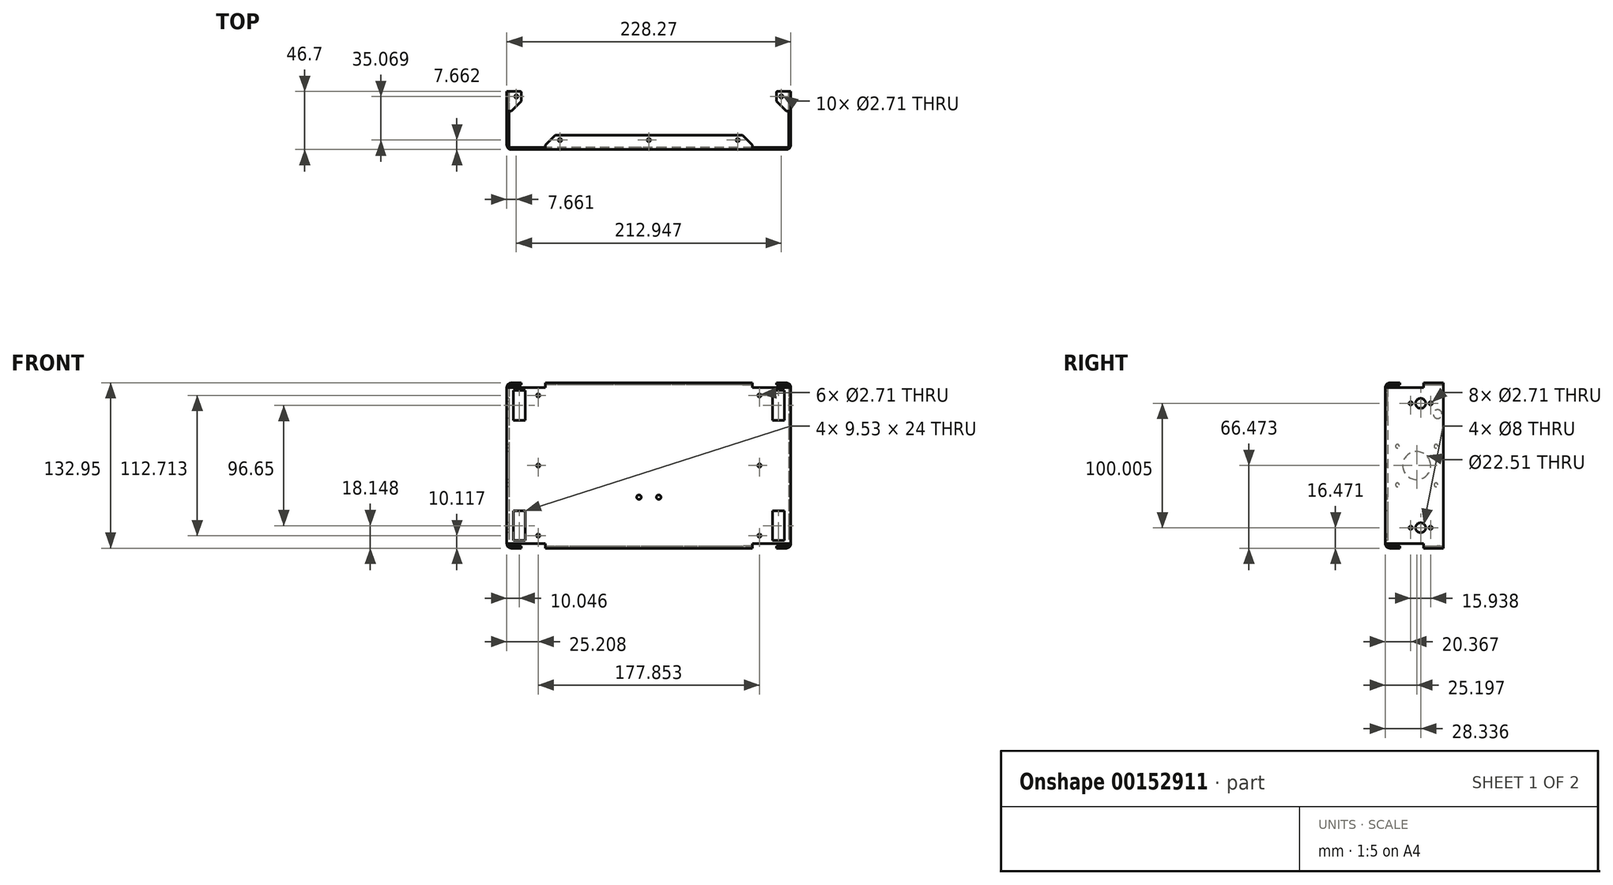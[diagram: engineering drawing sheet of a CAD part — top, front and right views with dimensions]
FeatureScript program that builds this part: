
annotation { "Feature Type Name" : "Feature", "Feature Type Description" : "" }
export const myFeature = defineFeature(function(context is Context, id is Id, definition is map)
    precondition{}
    {
        {
            var Q0;
            Q0=qCreatedBy(makeId("Top.planeOp"),FACE);
            var sketch = newSketch(context, id + "F0", { "sketchPlane" : qUnion([Q0])});
            skLineSegment(sketch, "E0.bottom", {"start": v(0, 0) * mm, "end": v(-224.85, 0) * mm});
            skLineSegment(sketch, "E0.top", {"start": v(1.7, -1.7) * mm, "end": v(-226.56, -1.7) * mm});
            skLineSegment(sketch, "E1.top", {"start": v(-224.85, 44.99) * mm, "end": v(-226.56, 44.99) * mm});
            skLineSegment(sketch, "E1.left", {"start": v(-224.85, 0) * mm, "end": v(-224.85, 44.99) * mm});
            skLineSegment(sketch, "E1.right", {"start": v(-226.56, -1.7) * mm, "end": v(-226.56, 44.99) * mm});
            skLineSegment(sketch, "E2.top", {"start": v(0, 44.99) * mm, "end": v(1.7, 44.99) * mm});
            skLineSegment(sketch, "E2.left", {"start": v(0, 0) * mm, "end": v(0, 44.99) * mm});
            skLineSegment(sketch, "E2.right", {"start": v(1.7, -1.7) * mm, "end": v(1.7, 44.99) * mm});
            skLineSegment(sketch, "E3", {"start": v(-112.43, 0) * mm, "end": v(-112.43, -1.7) * mm, "construction": true});
            skSolve(sketch);
        }
        {
            var Q0;
            Q0 = qSketchRegion(id + "F0", true);
            extrude(context, id + "F1", {"entities" : qUnion([Q0]), "depth" : 125.57 * mm});
        }
        {
            var Q0;
            Q0=makeQuery(id+"F1.opExtrude","CAP_FACE",FACE,{"disambiguationData":[OSD([sQuery(id+"F0.wireOp",EDGE,"E0.bottom"),sQuery(id+"F0.wireOp",EDGE,"E0.top"),sQuery(id+"F0.wireOp",EDGE,"E1.top"),sQuery(id+"F0.wireOp",EDGE,"E1.left"),sQuery(id+"F0.wireOp",EDGE,"E1.right"),sQuery(id+"F0.wireOp",EDGE,"E2.top"),sQuery(id+"F0.wireOp",EDGE,"E2.left"),sQuery(id+"F0.wireOp",EDGE,"E2.right")])],"isStart":true});
            var sketch = newSketch(context, id + "F2", { "sketchPlane" : qUnion([Q0])});
            skLineSegment(sketch, "E4.bottom", {"start": v(1.7, -44.99) * mm, "end": v(0, -44.99) * mm});
            skLineSegment(sketch, "E4.top", {"start": v(1.7, -29.11) * mm, "end": v(0, -29.11) * mm});
            skLineSegment(sketch, "E4.left", {"start": v(1.7, -44.99) * mm, "end": v(1.7, -29.11) * mm});
            skLineSegment(sketch, "E4.right", {"start": v(0, -44.99) * mm, "end": v(0, -29.11) * mm});
            skLineSegment(sketch, "E5.bottom", {"start": v(-29.11, 0) * mm, "end": v(-195.74, 0) * mm});
            skLineSegment(sketch, "E5.top", {"start": v(-29.11, 1.7) * mm, "end": v(-195.74, 1.7) * mm});
            skLineSegment(sketch, "E5.left", {"start": v(-29.11, 0) * mm, "end": v(-29.11, 1.7) * mm});
            skLineSegment(sketch, "E5.right", {"start": v(-195.74, 0) * mm, "end": v(-195.74, 1.7) * mm});
            skLineSegment(sketch, "E6.bottom", {"start": v(-224.85, -44.99) * mm, "end": v(-226.56, -44.99) * mm});
            skLineSegment(sketch, "E6.top", {"start": v(-224.85, -29.11) * mm, "end": v(-226.56, -29.11) * mm});
            skLineSegment(sketch, "E6.left", {"start": v(-224.85, -44.99) * mm, "end": v(-224.85, -29.11) * mm});
            skLineSegment(sketch, "E6.right", {"start": v(-226.56, -44.99) * mm, "end": v(-226.56, -29.11) * mm});
            skPoint(sketch, "E7", {"position": v(-112.43, 0) * mm});
            skLineSegment(sketch, "E8.top", {"start": v(-195.74, -29.11) * mm, "end": v(-224.85, -29.11) * mm, "construction": true});
            skLineSegment(sketch, "E8.left", {"start": v(-195.74, 0) * mm, "end": v(-195.74, -29.11) * mm, "construction": true});
            skSolve(sketch);
        }
        {
            var Q0;
            Q0 = qSketchRegion(id + "F2", true);
            extrude(context, id + "F3", {"entities" : qUnion([Q0]), "operationType" : NewBodyOperationType.ADD, "depth" : 3.7 * mm});
        }
        {
            var Q0;
            Q0=makeQuery(id+"F1.opExtrude","CAP_FACE",FACE,{"disambiguationData":[OSD([sQuery(id+"F0.wireOp",EDGE,"E0.bottom"),sQuery(id+"F0.wireOp",EDGE,"E0.top"),sQuery(id+"F0.wireOp",EDGE,"E1.top"),sQuery(id+"F0.wireOp",EDGE,"E1.left"),sQuery(id+"F0.wireOp",EDGE,"E1.right"),sQuery(id+"F0.wireOp",EDGE,"E2.top"),sQuery(id+"F0.wireOp",EDGE,"E2.left"),sQuery(id+"F0.wireOp",EDGE,"E2.right")])],"isStart":false});
            var sketch = newSketch(context, id + "F4", { "sketchPlane" : qUnion([Q0])});
            skLineSegment(sketch, "E9.bottom", {"start": v(-226.56, 44.99) * mm, "end": v(-224.85, 44.99) * mm});
            skLineSegment(sketch, "E9.top", {"start": v(-226.56, 29.11) * mm, "end": v(-224.85, 29.11) * mm});
            skLineSegment(sketch, "E9.left", {"start": v(-226.56, 44.99) * mm, "end": v(-226.56, 29.11) * mm});
            skLineSegment(sketch, "E9.right", {"start": v(-224.85, 44.99) * mm, "end": v(-224.85, 29.11) * mm});
            skLineSegment(sketch, "E10.bottom", {"start": v(0, 44.99) * mm, "end": v(1.7, 44.99) * mm});
            skLineSegment(sketch, "E10.top", {"start": v(0, 29.11) * mm, "end": v(1.7, 29.11) * mm});
            skLineSegment(sketch, "E10.left", {"start": v(0, 44.99) * mm, "end": v(0, 29.11) * mm});
            skLineSegment(sketch, "E10.right", {"start": v(1.7, 44.99) * mm, "end": v(1.7, 29.11) * mm});
            skLineSegment(sketch, "E11.bottom", {"start": v(-29.11, -1.7) * mm, "end": v(-195.74, -1.7) * mm});
            skLineSegment(sketch, "E11.top", {"start": v(-29.11, 0) * mm, "end": v(-195.74, 0) * mm});
            skLineSegment(sketch, "E11.left", {"start": v(-29.11, -1.7) * mm, "end": v(-29.11, 0) * mm});
            skLineSegment(sketch, "E11.right", {"start": v(-195.74, -1.7) * mm, "end": v(-195.74, 0) * mm});
            skSolve(sketch);
        }
        {
            var Q0;
            Q0 = qSketchRegion(id + "F4", true);
            extrude(context, id + "F5", {"entities" : qUnion([Q0]), "operationType" : NewBodyOperationType.ADD, "depth" : 3.7 * mm});
        }
        {
            var Q0;
            Q0=makeQuery(id+"F5.boolean.opBoolean","MERGE",FACE,{"derivedFrom":[makeQuery(id+"F3.boolean.opBoolean","MERGE",FACE,{"derivedFrom":[makeQuery(id+"F1.opExtrude","SWEPT_FACE",FACE,{"disambiguationData":[OSD([sQuery(id+"F0.wireOp",EDGE,"E0.bottom")])]}),makeQuery(id+"F3.opExtrude","SWEPT_FACE",FACE,{"disambiguationData":[OSD([sQuery(id+"F2.wireOp",EDGE,"E5.bottom")])]})]}),makeQuery(id+"F5.opExtrude","SWEPT_FACE",FACE,{"disambiguationData":[OSD([sQuery(id+"F4.wireOp",EDGE,"E11.top")])]})]});
            var sketch = newSketch(context, id + "F6", { "sketchPlane" : qUnion([Q0])});
            skLineSegment(sketch, "E12.bottom", {"start": v(195.74, -3.7) * mm, "end": v(29.11, -3.7) * mm});
            skLineSegment(sketch, "E12.top", {"start": v(195.74, -1.98) * mm, "end": v(29.11, -1.98) * mm});
            skLineSegment(sketch, "E12.left", {"start": v(195.74, -3.7) * mm, "end": v(195.74, -1.98) * mm});
            skLineSegment(sketch, "E12.right", {"start": v(29.11, -3.7) * mm, "end": v(29.11, -1.98) * mm});
            skLineSegment(sketch, "E13.bottom", {"start": v(29.11, 129.26) * mm, "end": v(195.74, 129.26) * mm});
            skLineSegment(sketch, "E13.top", {"start": v(29.11, 127.55) * mm, "end": v(195.74, 127.55) * mm});
            skLineSegment(sketch, "E13.left", {"start": v(29.11, 129.26) * mm, "end": v(29.11, 127.55) * mm});
            skLineSegment(sketch, "E13.right", {"start": v(195.74, 129.26) * mm, "end": v(195.74, 127.55) * mm});
            skSolve(sketch);
        }
        {
            var Q0;
            Q0 = qSketchRegion(id + "F6", true);
            extrude(context, id + "F7", {"entities" : qUnion([Q0]), "operationType" : NewBodyOperationType.ADD, "depth" : 9.92 * mm});
        }
        {
            var Q0;
            Q0=makeQuery(id+"F5.boolean.opBoolean","MERGE",FACE,{"derivedFrom":[makeQuery(id+"F3.boolean.opBoolean","MERGE",FACE,{"derivedFrom":[makeQuery(id+"F1.opExtrude","SWEPT_FACE",FACE,{"disambiguationData":[OSD([sQuery(id+"F0.wireOp",EDGE,"E1.left")])]}),makeQuery(id+"F3.opExtrude","SWEPT_FACE",FACE,{"disambiguationData":[OSD([sQuery(id+"F2.wireOp",EDGE,"E6.left")])]})]}),makeQuery(id+"F5.opExtrude","SWEPT_FACE",FACE,{"disambiguationData":[OSD([sQuery(id+"F4.wireOp",EDGE,"E9.right")])]})]});
            var sketch = newSketch(context, id + "F8", { "sketchPlane" : qUnion([Q0])});
            skLineSegment(sketch, "E14.bottom", {"start": v(29.11, 129.26) * mm, "end": v(44.99, 129.26) * mm});
            skLineSegment(sketch, "E14.top", {"start": v(29.11, 127.55) * mm, "end": v(44.99, 127.55) * mm});
            skLineSegment(sketch, "E14.left", {"start": v(29.11, 129.26) * mm, "end": v(29.11, 127.55) * mm});
            skLineSegment(sketch, "E14.right", {"start": v(44.99, 129.26) * mm, "end": v(44.99, 127.55) * mm});
            skLineSegment(sketch, "E15.bottom", {"start": v(29.11, -3.7) * mm, "end": v(44.99, -3.7) * mm});
            skLineSegment(sketch, "E15.top", {"start": v(29.11, -1.98) * mm, "end": v(44.99, -1.98) * mm});
            skLineSegment(sketch, "E15.left", {"start": v(29.11, -3.7) * mm, "end": v(29.11, -1.98) * mm});
            skLineSegment(sketch, "E15.right", {"start": v(44.99, -3.7) * mm, "end": v(44.99, -1.98) * mm});
            skSolve(sketch);
        }
        {
            var Q0;
            Q0 = qSketchRegion(id + "F8", true);
            extrude(context, id + "F9", {"entities" : qUnion([Q0]), "operationType" : NewBodyOperationType.ADD, "depth" : 9.92 * mm});
        }
        {
            var Q0;
            Q0=makeQuery(id+"F5.boolean.opBoolean","MERGE",FACE,{"derivedFrom":[makeQuery(id+"F3.boolean.opBoolean","MERGE",FACE,{"derivedFrom":[makeQuery(id+"F1.opExtrude","SWEPT_FACE",FACE,{"disambiguationData":[OSD([sQuery(id+"F0.wireOp",EDGE,"E2.left")])]}),makeQuery(id+"F3.opExtrude","SWEPT_FACE",FACE,{"disambiguationData":[OSD([sQuery(id+"F2.wireOp",EDGE,"E4.right")])]})]}),makeQuery(id+"F5.opExtrude","SWEPT_FACE",FACE,{"disambiguationData":[OSD([sQuery(id+"F4.wireOp",EDGE,"E10.left")])]})]});
            var sketch = newSketch(context, id + "F10", { "sketchPlane" : qUnion([Q0])});
            skLineSegment(sketch, "E16.bottom", {"start": v(-29.11, -3.7) * mm, "end": v(-44.99, -3.7) * mm});
            skLineSegment(sketch, "E16.top", {"start": v(-29.11, -1.98) * mm, "end": v(-44.99, -1.98) * mm});
            skLineSegment(sketch, "E16.left", {"start": v(-29.11, -3.7) * mm, "end": v(-29.11, -1.98) * mm});
            skLineSegment(sketch, "E16.right", {"start": v(-44.99, -3.7) * mm, "end": v(-44.99, -1.98) * mm});
            skLineSegment(sketch, "E17.bottom", {"start": v(-29.11, 129.26) * mm, "end": v(-44.99, 129.26) * mm});
            skLineSegment(sketch, "E17.top", {"start": v(-29.11, 127.55) * mm, "end": v(-44.99, 127.55) * mm});
            skLineSegment(sketch, "E17.left", {"start": v(-29.11, 129.26) * mm, "end": v(-29.11, 127.55) * mm});
            skLineSegment(sketch, "E17.right", {"start": v(-44.99, 129.26) * mm, "end": v(-44.99, 127.55) * mm});
            skSolve(sketch);
        }
        {
            var Q0;
            Q0 = qSketchRegion(id + "F10", true);
            extrude(context, id + "F11", {"entities" : qUnion([Q0]), "operationType" : NewBodyOperationType.ADD, "depth" : 9.92 * mm});
        }
        {
            var Q0;
            Q0=makeQuery(id+"F11.opExtrude","CAP_EDGE",EDGE,{"disambiguationData":[OSD([sQuery(id+"F10.wireOp",EDGE,"E17.top")])],"isStart":true});
            var Q1;
            Q1=makeQuery(id+"F7.opExtrude","CAP_EDGE",EDGE,{"disambiguationData":[OSD([sQuery(id+"F6.wireOp",EDGE,"E13.top")])],"isStart":true});
            var Q2;
            Q2=makeQuery(id+"F9.opExtrude","CAP_EDGE",EDGE,{"disambiguationData":[OSD([sQuery(id+"F8.wireOp",EDGE,"E14.top")])],"isStart":true});
            var Q3;
            Q3=makeQuery(id+"F9.opExtrude","CAP_EDGE",EDGE,{"disambiguationData":[OSD([sQuery(id+"F8.wireOp",EDGE,"E15.top")])],"isStart":true});
            var Q4;
            Q4=makeQuery(id+"F7.opExtrude","CAP_EDGE",EDGE,{"disambiguationData":[OSD([sQuery(id+"F6.wireOp",EDGE,"E12.top")])],"isStart":true});
            var Q5;
            Q5=makeQuery(id+"F11.opExtrude","CAP_EDGE",EDGE,{"disambiguationData":[OSD([sQuery(id+"F10.wireOp",EDGE,"E16.top")])],"isStart":true});
            var Q6;
            Q6=makeQuery(id+"F1.opExtrude","SWEPT_EDGE",EDGE,{"disambiguationData":[OSD([sQuery(id+"F0.wireOp",EDGE,"E0.bottom"),sQuery(id+"F0.wireOp",EDGE,"E2.left")])]});
            var Q7;
            Q7=makeQuery(id+"F1.opExtrude","SWEPT_EDGE",EDGE,{"disambiguationData":[OSD([sQuery(id+"F0.wireOp",EDGE,"E0.bottom"),sQuery(id+"F0.wireOp",EDGE,"E1.left")])]});
            fillet(context, id + "F12", {"entities" : qUnion([Q0, Q1, Q2, Q3, Q4, Q5, Q6, Q7]), "radius" : 1.98 * mm, "tangentPropagation" : true, "allowEdgeOverflow" : false});
        }
        {
            var Q0;
            Q0=makeQuery(id+"F3.opExtrude","CAP_EDGE",EDGE,{"disambiguationData":[OSD([sQuery(id+"F2.wireOp",EDGE,"E6.right")])],"isStart":false});
            var Q1;
            Q1=makeQuery(id+"F3.opExtrude","CAP_EDGE",EDGE,{"disambiguationData":[OSD([sQuery(id+"F2.wireOp",EDGE,"E5.top")])],"isStart":false});
            var Q2;
            Q2=makeQuery(id+"F1.opExtrude","SWEPT_EDGE",EDGE,{"disambiguationData":[OSD([sQuery(id+"F0.wireOp",EDGE,"E0.top"),sQuery(id+"F0.wireOp",EDGE,"E1.right")])]});
            var Q3;
            Q3=makeQuery(id+"F5.opExtrude","CAP_EDGE",EDGE,{"disambiguationData":[OSD([sQuery(id+"F4.wireOp",EDGE,"E11.bottom")])],"isStart":false});
            var Q4;
            Q4=makeQuery(id+"F5.opExtrude","CAP_EDGE",EDGE,{"disambiguationData":[OSD([sQuery(id+"F4.wireOp",EDGE,"E9.left")])],"isStart":false});
            var Q5;
            Q5=makeQuery(id+"F3.opExtrude","CAP_EDGE",EDGE,{"disambiguationData":[OSD([sQuery(id+"F2.wireOp",EDGE,"E4.left")])],"isStart":false});
            var Q6;
            Q6=makeQuery(id+"F1.opExtrude","SWEPT_EDGE",EDGE,{"disambiguationData":[OSD([sQuery(id+"F0.wireOp",EDGE,"E0.top"),sQuery(id+"F0.wireOp",EDGE,"E2.right")])]});
            var Q7;
            Q7=makeQuery(id+"F5.opExtrude","CAP_EDGE",EDGE,{"disambiguationData":[OSD([sQuery(id+"F4.wireOp",EDGE,"E10.right")])],"isStart":false});
            fillet(context, id + "F13", {"entities" : qUnion([Q0, Q1, Q2, Q3, Q4, Q5, Q6, Q7]), "radius" : 3.7 * mm, "tangentPropagation" : true, "allowEdgeOverflow" : false});
        }
        {
            var Q0;
            Q0=makeQuery(id+"F9.opExtrude","CAP_EDGE",EDGE,{"disambiguationData":[OSD([sQuery(id+"F8.wireOp",EDGE,"E14.left")])],"isStart":false});
            var Q1;
            Q1=makeQuery(id+"F7.opExtrude","CAP_EDGE",EDGE,{"disambiguationData":[OSD([sQuery(id+"F6.wireOp",EDGE,"E13.right")])],"isStart":false});
            var Q2;
            Q2=makeQuery(id+"F7.opExtrude","CAP_EDGE",EDGE,{"disambiguationData":[OSD([sQuery(id+"F6.wireOp",EDGE,"E13.left")])],"isStart":false});
            var Q3;
            Q3=makeQuery(id+"F11.opExtrude","CAP_EDGE",EDGE,{"disambiguationData":[OSD([sQuery(id+"F10.wireOp",EDGE,"E17.left")])],"isStart":false});
            var Q4;
            Q4=makeQuery(id+"F7.opExtrude","CAP_EDGE",EDGE,{"disambiguationData":[OSD([sQuery(id+"F6.wireOp",EDGE,"E12.right")])],"isStart":false});
            var Q5;
            Q5=makeQuery(id+"F11.opExtrude","CAP_EDGE",EDGE,{"disambiguationData":[OSD([sQuery(id+"F10.wireOp",EDGE,"E16.left")])],"isStart":false});
            var Q6;
            Q6=makeQuery(id+"F9.opExtrude","CAP_EDGE",EDGE,{"disambiguationData":[OSD([sQuery(id+"F8.wireOp",EDGE,"E15.left")])],"isStart":false});
            var Q7;
            Q7=makeQuery(id+"F7.opExtrude","CAP_EDGE",EDGE,{"disambiguationData":[OSD([sQuery(id+"F6.wireOp",EDGE,"E12.left")])],"isStart":false});
            chamfer(context, id + "F14", {"entities" : qUnion([Q0, Q1, Q2, Q3, Q4, Q5, Q6, Q7]), "width" : 7.94 * mm, "tangentPropagation" : true});
        }
        {
            var Q0;
            Q0=makeQuery(id+"F7.boolean.opBoolean","MERGE",FACE,{"derivedFrom":[makeQuery(id+"F3.opExtrude","CAP_FACE",FACE,{"disambiguationData":[OSD([sQuery(id+"F2.wireOp",EDGE,"E5.bottom"),sQuery(id+"F2.wireOp",EDGE,"E5.top"),sQuery(id+"F2.wireOp",EDGE,"E5.left"),sQuery(id+"F2.wireOp",EDGE,"E5.right")])],"isStart":false}),makeQuery(id+"F7.opExtrude","SWEPT_FACE",FACE,{"disambiguationData":[OSD([sQuery(id+"F6.wireOp",EDGE,"E12.bottom")])]})]});
            var sketch = newSketch(context, id + "F15", { "sketchPlane" : qUnion([Q0])});
            skLineSegment(sketch, "E18", {"start": v(-33.08, -5.95) * mm, "end": v(-41.02, -5.95) * mm, "construction": true});
            skLineSegment(sketch, "E19", {"start": v(-41.02, -5.95) * mm, "end": v(-112.43, -5.95) * mm, "construction": true});
            skLineSegment(sketch, "E20", {"start": v(-112.43, -5.95) * mm, "end": v(-183.83, -5.95) * mm, "construction": true});
            skLineSegment(sketch, "E21", {"start": v(-183.83, -5.95) * mm, "end": v(-191.77, -5.95) * mm, "construction": true});
            skCircle(sketch, "E22", {"center": v(-41.02, -5.95) * mm, "radius": 1.35 * mm});
            skCircle(sketch, "E23", {"center": v(-112.43, -5.95) * mm, "radius": 1.35 * mm});
            skCircle(sketch, "E24", {"center": v(-183.83, -5.95) * mm, "radius": 1.35 * mm});
            skLineSegment(sketch, "E25", {"start": v(-5.95, -33.08) * mm, "end": v(-5.95, -41.02) * mm, "construction": true});
            skLineSegment(sketch, "E26", {"start": v(-218.9, -33.08) * mm, "end": v(-218.9, -41.02) * mm, "construction": true});
            skCircle(sketch, "E27", {"center": v(-218.9, -41.02) * mm, "radius": 1.35 * mm});
            skCircle(sketch, "E28", {"center": v(-5.95, -41.02) * mm, "radius": 1.35 * mm});
            skSolve(sketch);
        }
        {
            var Q0;
            Q0 = qSketchRegion(id + "F15", true);
            var Q1;
            Q1=makeQuery(id+"F7.boolean.opBoolean","MERGE",FACE,{"derivedFrom":[makeQuery(id+"F5.opExtrude","CAP_FACE",FACE,{"disambiguationData":[OSD([sQuery(id+"F4.wireOp",EDGE,"E11.bottom"),sQuery(id+"F4.wireOp",EDGE,"E11.top"),sQuery(id+"F4.wireOp",EDGE,"E11.left"),sQuery(id+"F4.wireOp",EDGE,"E11.right")])],"isStart":false}),makeQuery(id+"F7.opExtrude","SWEPT_FACE",FACE,{"disambiguationData":[OSD([sQuery(id+"F6.wireOp",EDGE,"E13.bottom")])]})]});
            extrude(context, id + "F16", {"entities" : qUnion([Q0]), "operationType" : NewBodyOperationType.REMOVE, "endBound" : BoundingType.UP_TO_SURFACE, "oppositeDirection" : true, "endBoundEntityFace" : qUnion([Q1]), "depth" : 25.4 * mm});
        }
        {
            var Q0;
            Q0=makeQuery(id+"F5.boolean.opBoolean","MERGE",FACE,{"derivedFrom":[makeQuery(id+"F3.boolean.opBoolean","MERGE",FACE,{"derivedFrom":[makeQuery(id+"F1.opExtrude","SWEPT_FACE",FACE,{"disambiguationData":[OSD([sQuery(id+"F0.wireOp",EDGE,"E0.top")])]}),makeQuery(id+"F3.opExtrude","SWEPT_FACE",FACE,{"disambiguationData":[OSD([sQuery(id+"F2.wireOp",EDGE,"E5.top")])]})]}),makeQuery(id+"F5.opExtrude","SWEPT_FACE",FACE,{"disambiguationData":[OSD([sQuery(id+"F4.wireOp",EDGE,"E11.bottom")])]})]});
            var sketch = newSketch(context, id + "F17", { "sketchPlane" : qUnion([Q0])});
            skLineSegment(sketch, "E29.bottom", {"start": v(-221.28, 2.46) * mm, "end": v(-211.75, 2.46) * mm});
            skLineSegment(sketch, "E29.top", {"start": v(-221.28, 26.46) * mm, "end": v(-211.75, 26.46) * mm});
            skLineSegment(sketch, "E29.left", {"start": v(-221.28, 2.46) * mm, "end": v(-221.28, 26.46) * mm});
            skLineSegment(sketch, "E29.right", {"start": v(-211.75, 2.46) * mm, "end": v(-211.75, 26.46) * mm});
            skLineSegment(sketch, "E30.bottom", {"start": v(-221.28, 123.1) * mm, "end": v(-211.75, 123.1) * mm});
            skLineSegment(sketch, "E30.top", {"start": v(-221.28, 99.1) * mm, "end": v(-211.75, 99.1) * mm});
            skLineSegment(sketch, "E30.left", {"start": v(-221.28, 123.1) * mm, "end": v(-221.28, 99.1) * mm});
            skLineSegment(sketch, "E30.right", {"start": v(-211.75, 123.1) * mm, "end": v(-211.75, 99.1) * mm});
            skLineSegment(sketch, "E31.bottom", {"start": v(-13.1, 123.1) * mm, "end": v(-3.57, 123.1) * mm});
            skLineSegment(sketch, "E31.top", {"start": v(-13.1, 99.1) * mm, "end": v(-3.57, 99.1) * mm});
            skLineSegment(sketch, "E31.left", {"start": v(-13.1, 123.1) * mm, "end": v(-13.1, 99.1) * mm});
            skLineSegment(sketch, "E31.right", {"start": v(-3.57, 123.1) * mm, "end": v(-3.57, 99.1) * mm});
            skLineSegment(sketch, "E32.bottom", {"start": v(-3.57, 2.46) * mm, "end": v(-13.1, 2.46) * mm});
            skLineSegment(sketch, "E32.top", {"start": v(-3.57, 26.46) * mm, "end": v(-13.1, 26.46) * mm});
            skLineSegment(sketch, "E32.left", {"start": v(-3.57, 2.46) * mm, "end": v(-3.57, 26.46) * mm});
            skLineSegment(sketch, "E32.right", {"start": v(-13.1, 2.46) * mm, "end": v(-13.1, 26.46) * mm});
            skLineSegment(sketch, "E33", {"start": v(-3.57, 2.46) * mm, "end": v(-3.57, 0) * mm, "construction": true});
            skLineSegment(sketch, "E34", {"start": v(-3.57, 2.46) * mm, "end": v(-1.98, 2.46) * mm, "construction": true});
            skLineSegment(sketch, "E35", {"start": v(-112.43, 0) * mm, "end": v(-112.43, 125.57) * mm, "construction": true});
            skLineSegment(sketch, "E36.bottom", {"start": v(-13.1, 26.46) * mm, "end": v(-211.75, 26.46) * mm, "construction": true});
            skLineSegment(sketch, "E36.top", {"start": v(-13.1, 99.1) * mm, "end": v(-211.75, 99.1) * mm, "construction": true});
            skLineSegment(sketch, "E36.left", {"start": v(-13.1, 26.46) * mm, "end": v(-13.1, 99.1) * mm, "construction": true});
            skLineSegment(sketch, "E36.right", {"start": v(-211.75, 26.46) * mm, "end": v(-211.75, 99.1) * mm, "construction": true});
            skPoint(sketch, "E37", {"position": v(-8.34, 2.46) * mm});
            skLineSegment(sketch, "E38", {"start": v(-13.1, 123.1) * mm, "end": v(-23.5, 123.1) * mm, "construction": true});
            skLineSegment(sketch, "E39", {"start": v(-23.5, 123.1) * mm, "end": v(-23.5, 119.14) * mm, "construction": true});
            skLineSegment(sketch, "E40.bottom", {"start": v(-23.5, 119.14) * mm, "end": v(-201.35, 119.14) * mm, "construction": true});
            skLineSegment(sketch, "E40.top", {"start": v(-23.5, 6.43) * mm, "end": v(-201.35, 6.43) * mm, "construction": true});
            skLineSegment(sketch, "E40.left", {"start": v(-23.5, 119.14) * mm, "end": v(-23.5, 6.43) * mm, "construction": true});
            skLineSegment(sketch, "E40.right", {"start": v(-201.35, 119.14) * mm, "end": v(-201.35, 6.43) * mm, "construction": true});
            skCircle(sketch, "E41", {"center": v(-23.5, 119.14) * mm, "radius": 1.35 * mm});
            skCircle(sketch, "E42", {"center": v(-23.5, 6.43) * mm, "radius": 1.35 * mm});
            skCircle(sketch, "E43", {"center": v(-201.35, 6.43) * mm, "radius": 1.35 * mm});
            skCircle(sketch, "E44", {"center": v(-201.35, 119.14) * mm, "radius": 1.35 * mm});
            skCircle(sketch, "E45", {"center": v(-23.5, 62.78) * mm, "radius": 1.35 * mm});
            skCircle(sketch, "E46", {"center": v(-201.35, 62.78) * mm, "radius": 1.35 * mm});
            skPoint(sketch, "E47", {"position": v(-216.51, 2.46) * mm});
            skLineSegment(sketch, "E48", {"start": v(-112.43, 62.78) * mm, "end": v(-120.36, 62.78) * mm, "construction": true});
            skLineSegment(sketch, "E49", {"start": v(-120.36, 62.78) * mm, "end": v(-120.36, 37.38) * mm, "construction": true});
            skLineSegment(sketch, "E50", {"start": v(-120.36, 37.38) * mm, "end": v(-112.43, 37.38) * mm, "construction": true});
            skLineSegment(sketch, "E51", {"start": v(-112.43, 37.38) * mm, "end": v(-104.49, 37.38) * mm, "construction": true});
            skCircle(sketch, "E52", {"center": v(-120.36, 37.38) * mm, "radius": 1.83 * mm});
            skCircle(sketch, "E53", {"center": v(-104.49, 37.38) * mm, "radius": 1.83 * mm});
            skSolve(sketch);
        }
        {
            var Q0;
            Q0 = qSketchRegion(id + "F17", true);
            var Q1;
            Q1=makeQuery(id+"F5.boolean.opBoolean","MERGE",FACE,{"derivedFrom":[makeQuery(id+"F3.boolean.opBoolean","MERGE",FACE,{"derivedFrom":[makeQuery(id+"F1.opExtrude","SWEPT_FACE",FACE,{"disambiguationData":[OSD([sQuery(id+"F0.wireOp",EDGE,"E0.bottom")])]}),makeQuery(id+"F3.opExtrude","SWEPT_FACE",FACE,{"disambiguationData":[OSD([sQuery(id+"F2.wireOp",EDGE,"E5.bottom")])]})]}),makeQuery(id+"F5.opExtrude","SWEPT_FACE",FACE,{"disambiguationData":[OSD([sQuery(id+"F4.wireOp",EDGE,"E11.top")])]})]});
            extrude(context, id + "F18", {"entities" : qUnion([Q0]), "operationType" : NewBodyOperationType.REMOVE, "endBound" : BoundingType.UP_TO_SURFACE, "oppositeDirection" : true, "endBoundEntityFace" : qUnion([Q1]), "depth" : 25.4 * mm});
        }
        {
            var Q0;
            Q0=makeQuery(id+"F5.boolean.opBoolean","MERGE",FACE,{"derivedFrom":[makeQuery(id+"F3.boolean.opBoolean","MERGE",FACE,{"derivedFrom":[makeQuery(id+"F1.opExtrude","SWEPT_FACE",FACE,{"disambiguationData":[OSD([sQuery(id+"F0.wireOp",EDGE,"E1.right")])]}),makeQuery(id+"F3.opExtrude","SWEPT_FACE",FACE,{"disambiguationData":[OSD([sQuery(id+"F2.wireOp",EDGE,"E6.right")])]})]}),makeQuery(id+"F5.opExtrude","SWEPT_FACE",FACE,{"disambiguationData":[OSD([sQuery(id+"F4.wireOp",EDGE,"E9.left")])]})]});
            var sketch = newSketch(context, id + "F19", { "sketchPlane" : qUnion([Q0])});
            skLineSegment(sketch, "E54", {"start": v(-44.99, 12.78) * mm, "end": v(-34.6, 12.78) * mm, "construction": true});
            skLineSegment(sketch, "E55", {"start": v(-34.6, 12.78) * mm, "end": v(-18.66, 12.78) * mm, "construction": true});
            skLineSegment(sketch, "E56", {"start": v(-34.6, 12.78) * mm, "end": v(-34.6, 0) * mm, "construction": true});
            skLineSegment(sketch, "E57", {"start": v(-34.6, 125.57) * mm, "end": v(-34.6, 112.79) * mm, "construction": true});
            skLineSegment(sketch, "E58", {"start": v(-34.6, 112.79) * mm, "end": v(-18.66, 112.79) * mm, "construction": true});
            skCircle(sketch, "E59", {"center": v(-34.6, 12.78) * mm, "radius": 1.35 * mm});
            skCircle(sketch, "E60", {"center": v(-18.66, 12.78) * mm, "radius": 1.35 * mm});
            skCircle(sketch, "E61", {"center": v(-18.66, 112.79) * mm, "radius": 1.35 * mm});
            skCircle(sketch, "E62", {"center": v(-34.6, 112.79) * mm, "radius": 1.35 * mm});
            skCircle(sketch, "E63", {"center": v(-26.63, 112.79) * mm, "radius": 4 * mm});
            skCircle(sketch, "E64", {"center": v(-26.63, 12.78) * mm, "radius": 4 * mm});
            skCircle(sketch, "E65", {"center": v(-34.6, 12.78) * mm, "radius": 3.97 * mm, "construction": true});
            skLineSegment(sketch, "E66", {"start": v(-26.63, 112.79) * mm, "end": v(-26.63, 12.78) * mm, "construction": true});
            skLineSegment(sketch, "E67", {"start": v(-26.63, 62.78) * mm, "end": v(-1.98, 62.78) * mm, "construction": true});
            skSolve(sketch);
        }
        {
            var Q0;
            Q0 = qSketchRegion(id + "F19", true);
            var Q1;
            Q1=makeQuery(id+"F5.boolean.opBoolean","MERGE",FACE,{"derivedFrom":[makeQuery(id+"F3.boolean.opBoolean","MERGE",FACE,{"derivedFrom":[makeQuery(id+"F1.opExtrude","SWEPT_FACE",FACE,{"disambiguationData":[OSD([sQuery(id+"F0.wireOp",EDGE,"E2.right")])]}),makeQuery(id+"F3.opExtrude","SWEPT_FACE",FACE,{"disambiguationData":[OSD([sQuery(id+"F2.wireOp",EDGE,"E4.left")])]})]}),makeQuery(id+"F5.opExtrude","SWEPT_FACE",FACE,{"disambiguationData":[OSD([sQuery(id+"F4.wireOp",EDGE,"E10.right")])]})]});
            extrude(context, id + "F20", {"entities" : qUnion([Q0]), "operationType" : NewBodyOperationType.REMOVE, "endBound" : BoundingType.UP_TO_SURFACE, "oppositeDirection" : true, "endBoundEntityFace" : qUnion([Q1]), "depth" : 25.4 * mm});
        }
        {
            var Q0;
            Q0=makeQuery(id+"F9.opExtrude","CAP_EDGE",EDGE,{"disambiguationData":[OSD([sQuery(id+"F8.wireOp",EDGE,"E15.right")])],"isStart":false});
            var Q1;
            Q1=makeQuery(id+"F9.opExtrude","CAP_EDGE",EDGE,{"disambiguationData":[OSD([sQuery(id+"F8.wireOp",EDGE,"E14.right")])],"isStart":false});
            var Q2;
            Q2=makeQuery(id+"F11.opExtrude","CAP_EDGE",EDGE,{"disambiguationData":[OSD([sQuery(id+"F10.wireOp",EDGE,"E17.right")])],"isStart":false});
            var Q3;
            Q3=makeQuery(id+"F11.opExtrude","CAP_EDGE",EDGE,{"disambiguationData":[OSD([sQuery(id+"F10.wireOp",EDGE,"E16.right")])],"isStart":false});
            fillet(context, id + "F21", {"entities" : qUnion([Q0, Q1, Q2, Q3]), "radius" : 0.76 * mm, "tangentPropagation" : true, "allowEdgeOverflow" : false});
        }
        {
            var Q0;
            Q0=makeQuery(id+"F5.boolean.opBoolean","MERGE",FACE,{"derivedFrom":[makeQuery(id+"F3.boolean.opBoolean","MERGE",FACE,{"derivedFrom":[makeQuery(id+"F1.opExtrude","SWEPT_FACE",FACE,{"disambiguationData":[OSD([sQuery(id+"F0.wireOp",EDGE,"E1.right")])]}),makeQuery(id+"F3.opExtrude","SWEPT_FACE",FACE,{"disambiguationData":[OSD([sQuery(id+"F2.wireOp",EDGE,"E6.right")])]})]}),makeQuery(id+"F5.opExtrude","SWEPT_FACE",FACE,{"disambiguationData":[OSD([sQuery(id+"F4.wireOp",EDGE,"E9.left")])]})]});
            var sketch = newSketch(context, id + "F22", { "sketchPlane" : qUnion([Q0])});
            skLineSegment(sketch, "E68", {"start": v(-44.99, 62.78) * mm, "end": v(-23.49, 62.78) * mm, "construction": true});
            skLineSegment(sketch, "E69.bottom", {"start": v(-38.99, 78.28) * mm, "end": v(-7.99, 78.28) * mm, "construction": true});
            skLineSegment(sketch, "E69.top", {"start": v(-38.99, 47.28) * mm, "end": v(-7.99, 47.28) * mm, "construction": true});
            skLineSegment(sketch, "E69.left", {"start": v(-38.99, 78.28) * mm, "end": v(-38.99, 47.28) * mm, "construction": true});
            skLineSegment(sketch, "E69.right", {"start": v(-7.99, 78.28) * mm, "end": v(-7.99, 47.28) * mm, "construction": true});
            skPoint(sketch, "E69.middle", {"position": v(-23.49, 62.78) * mm});
            skCircle(sketch, "E70", {"center": v(-23.49, 62.78) * mm, "radius": 11.25 * mm});
            skCircle(sketch, "E71", {"center": v(-38.99, 78.28) * mm, "radius": 1.5 * mm});
            skCircle(sketch, "E72", {"center": v(-7.99, 78.28) * mm, "radius": 1.5 * mm});
            skCircle(sketch, "E73", {"center": v(-7.99, 47.28) * mm, "radius": 1.5 * mm});
            skCircle(sketch, "E74", {"center": v(-38.99, 47.28) * mm, "radius": 1.5 * mm});
            skLineSegment(sketch, "E75", {"start": v(-23.49, 104.15) * mm, "end": v(-23.49, 62.78) * mm, "construction": true});
            skLineSegment(sketch, "E76", {"start": v(-23.49, 104.15) * mm, "end": v(-40.24, 104.15) * mm, "construction": true});
            skLineSegment(sketch, "E77", {"start": v(-40.24, 104.15) * mm, "end": v(-44.99, 104.15) * mm, "construction": true});
            skCircle(sketch, "E78", {"center": v(-40.24, 104.15) * mm, "radius": 3.5 * mm});
            skCircle(sketch, "E79", {"center": v(-34.6, 112.79) * mm, "radius": 3.97 * mm, "construction": true});
            skCircle(sketch, "E80", {"center": v(-40.24, 104.15) * mm, "radius": 6.35 * mm, "construction": true});
            skSolve(sketch);
        }
        {
            var Q0;
            Q0 = qSketchRegion(id + "F22", true);
            var Q1;
            Q1=makeQuery(id+"F5.boolean.opBoolean","MERGE",FACE,{"derivedFrom":[makeQuery(id+"F3.boolean.opBoolean","MERGE",FACE,{"derivedFrom":[makeQuery(id+"F1.opExtrude","SWEPT_FACE",FACE,{"disambiguationData":[OSD([sQuery(id+"F0.wireOp",EDGE,"E1.left")])]}),makeQuery(id+"F3.opExtrude","SWEPT_FACE",FACE,{"disambiguationData":[OSD([sQuery(id+"F2.wireOp",EDGE,"E6.left")])]})]}),makeQuery(id+"F5.opExtrude","SWEPT_FACE",FACE,{"disambiguationData":[OSD([sQuery(id+"F4.wireOp",EDGE,"E9.right")])]})]});
            extrude(context, id + "F23", {"entities" : qUnion([Q0]), "operationType" : NewBodyOperationType.REMOVE, "endBound" : BoundingType.UP_TO_SURFACE, "oppositeDirection" : true, "endBoundEntityFace" : qUnion([Q1]), "depth" : 25.4 * mm});
        }
    });
